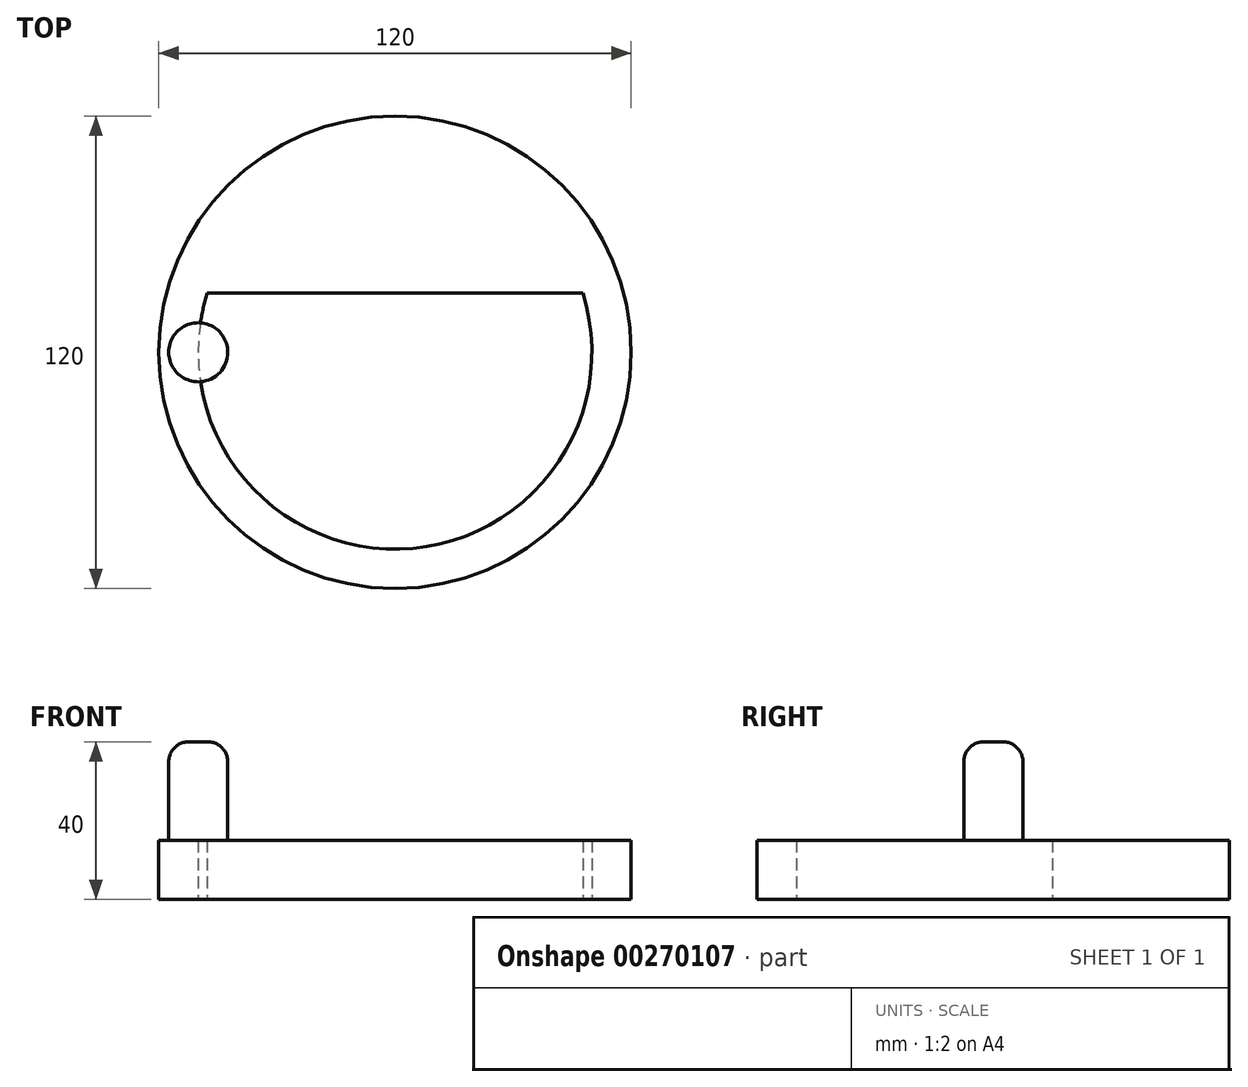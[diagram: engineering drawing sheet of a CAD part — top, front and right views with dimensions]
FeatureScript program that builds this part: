
annotation { "Feature Type Name" : "Feature", "Feature Type Description" : "" }
export const myFeature = defineFeature(function(context is Context, id is Id, definition is map)
    precondition{}
    {
        {
            var Q0;
            Q0=qCreatedBy(makeId("Top.planeOp"),FACE);
            var sketch = newSketch(context, id + "F0", { "sketchPlane" : qUnion([Q0])});
            skCircle(sketch, "E0", {"center": v(0, 0) * mm, "radius": 60 * mm});
            skCircle(sketch, "E1.0", {"center": v(0, 0) * mm, "radius": 50 * mm});
            skLineSegment(sketch, "E2.bottom", {"start": v(58.1, -15) * mm, "end": v(-58.1, -15) * mm});
            skLineSegment(sketch, "E2.top", {"start": v(58.1, 15) * mm, "end": v(-58.1, 15) * mm});
            skSolve(sketch);
        }
        {
            var Q0;
            Q0=makeQuery(id+"F0.imprint","IMPRINT",FACE,{"disambiguationData":[TD([[makeQuery(id+"F0.imprint","IMPRINT",EDGE,{"derivedFrom":sQuery(id+"F0.wireOp",EDGE,"E0")}),1.0]])]});
            var Q1;
            Q1=makeQuery(id+"F0.imprint","IMPRINT",FACE,{"disambiguationData":[TD([[makeQuery(id+"F0.imprint","IMPRINT",EDGE,{"derivedFrom":sQuery(id+"F0.wireOp",EDGE,"7yzDuP58-Arqv-ZxEu-qyVc-JEVxZBMYGXwJ.bottom")}),-1.0]])]});
            var Q2;
            {var subQ0=sQuery(id+"F0.wireOp",EDGE,"E2.top");var subQ1=sQuery(id+"F0.wireOp",EDGE,"E1.0");var subQ2=makeQuery(id+"F0.imprint","INTERSECT",VERTEX,{"disambiguationData":[OD(0.0)],"derivedFrom":[subQ1,subQ0]});Q2=makeQuery(id+"F0.imprint","IMPRINT",FACE,{"disambiguationData":[TD([[makeQuery(id+"F0.imprint","IMPRINT",EDGE,{"disambiguationData":[TD([[subQ2,-1.0]])],"derivedFrom":subQ1}),1.0]])]});}
            extrude(context, id + "F1", {"entities" : qUnion([Q0, Q1, Q2]), "depth" : 15 * mm});
        }
        {
            var Q0;
            Q0=makeQuery(id+"F1.opExtrude","CAP_FACE",FACE,{"disambiguationData":[OSD([sQuery(id+"F0.wireOp",EDGE,"E0"),sQuery(id+"F0.wireOp",EDGE,"E1.0"),sQuery(id+"F0.wireOp",EDGE,"E2.bottom"),sQuery(id+"F0.wireOp",EDGE,"E2.top")])],"isStart":false});
            var sketch = newSketch(context, id + "F2", { "sketchPlane" : qUnion([Q0])});
            skCircle(sketch, "E3", {"center": v(-50, 0) * mm, "radius": 7.5 * mm});
            skSolve(sketch);
        }
        {
            var Q0;
            Q0=makeQuery(id+"F2.imprint","IMPRINT",FACE,{"disambiguationData":[TD([[makeQuery(id+"F2.imprint","IMPRINT",EDGE,{"derivedFrom":sQuery(id+"F2.wireOp",EDGE,"E3")}),1.0]])]});
            extrude(context, id + "F3", {"entities" : qUnion([Q0]), "operationType" : NewBodyOperationType.ADD, "depth" : 25 * mm});
        }
        {
            var Q0;
            Q0=makeQuery(id+"F3.opExtrude","CAP_FACE",FACE,{"disambiguationData":[OSD([sQuery(id+"F2.wireOp",EDGE,"E3")])],"isStart":false});
            fillet(context, id + "F4", {"entities" : qUnion([Q0]), "radius" : 5 * mm, "tangentPropagation" : true, "allowEdgeOverflow" : false});
        }
        {
            var Q0;
            Q0=makeQuery(id+"F1.opExtrude","CAP_FACE",FACE,{"disambiguationData":[OSD([sQuery(id+"F0.wireOp",EDGE,"E0"),sQuery(id+"F0.wireOp",EDGE,"E1.0"),sQuery(id+"F0.wireOp",EDGE,"E2.bottom"),sQuery(id+"F0.wireOp",EDGE,"E2.top")])],"isStart":true});
            var sketch = newSketch(context, id + "F5", { "sketchPlane" : qUnion([Q0])});
            skLineSegment(sketch, "E4.bottom", {"start": v(4.12, -6.27) * mm, "end": v(-4.12, -6.27) * mm});
            skLineSegment(sketch, "E4.top", {"start": v(4.12, 6.27) * mm, "end": v(-4.12, 6.27) * mm});
            skLineSegment(sketch, "E4.left", {"start": v(4.12, -6.27) * mm, "end": v(4.12, 6.27) * mm});
            skLineSegment(sketch, "E4.right", {"start": v(-4.12, -6.27) * mm, "end": v(-4.12, 6.27) * mm});
            skPoint(sketch, "E4.middle", {"position": v(0, 0) * mm});
            skSolve(sketch);
        }
        {
            var Q0;
            Q0=makeQuery(id+"F5.imprint","IMPRINT",FACE,{"disambiguationData":[TD([[makeQuery(id+"F5.imprint","IMPRINT",EDGE,{"derivedFrom":sQuery(id+"F5.wireOp",EDGE,"E4.bottom")}),-1.0]])]});
            extrude(context, id + "F6", {"entities" : qUnion([Q0]), "operationType" : NewBodyOperationType.REMOVE, "oppositeDirection" : true, "depth" : 10 * mm});
        }
    });
